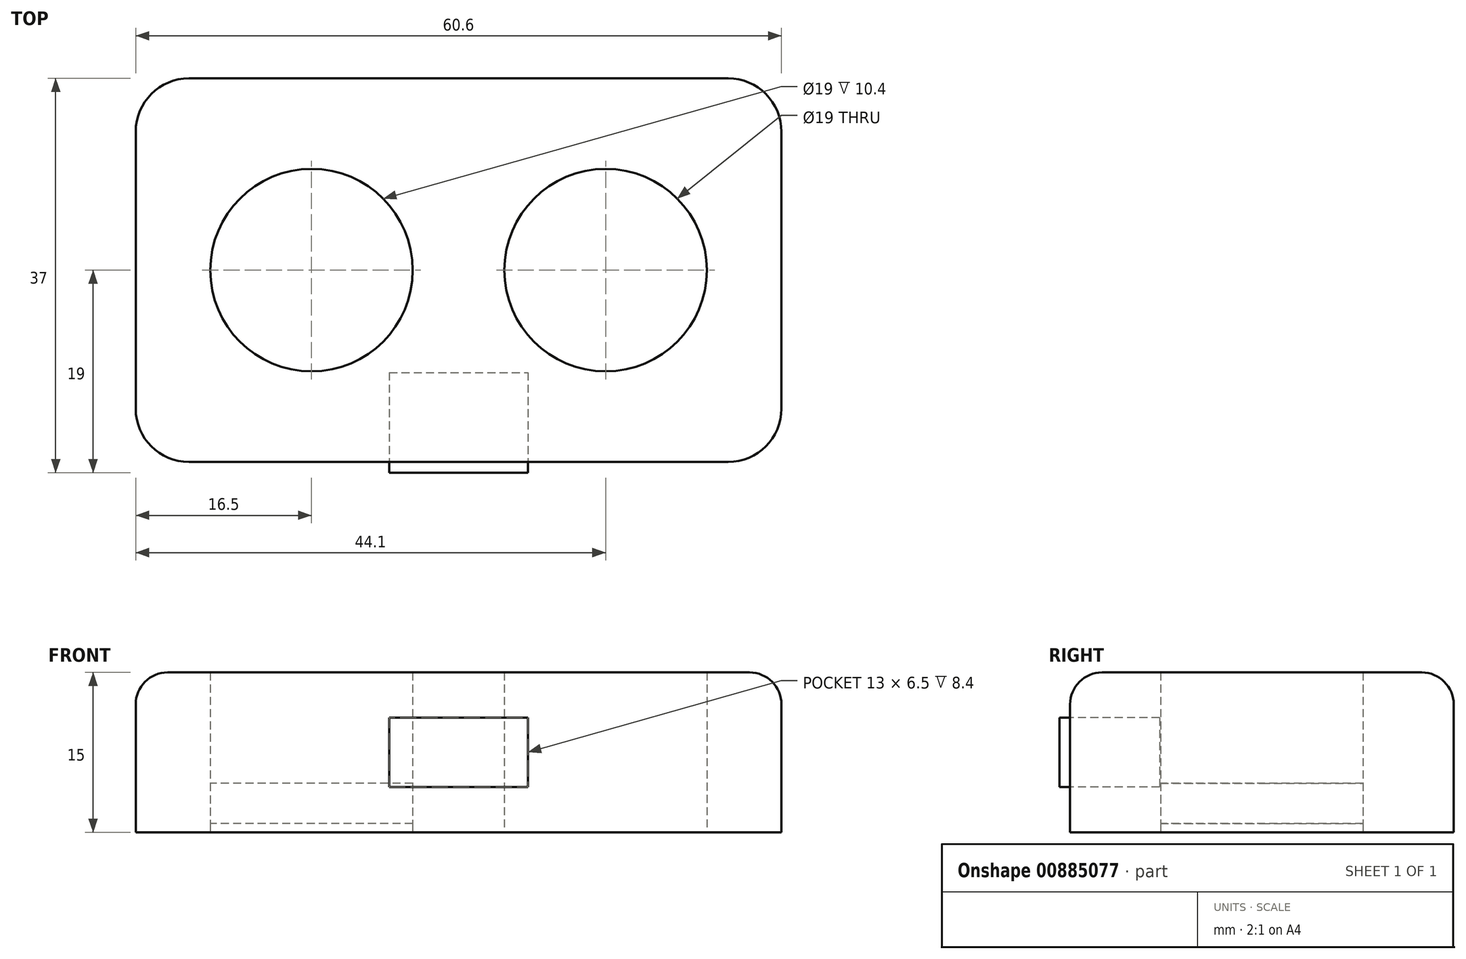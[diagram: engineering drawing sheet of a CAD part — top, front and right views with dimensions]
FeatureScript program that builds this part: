
annotation { "Feature Type Name" : "Feature", "Feature Type Description" : "" }
export const myFeature = defineFeature(function(context is Context, id is Id, definition is map)
    precondition{}
    {
        {
            var Q0;
            Q0=qCreatedBy(makeId("Top.planeOp"),FACE);
            var sketch = newSketch(context, id + "F0", { "sketchPlane" : qUnion([Q0])});
            skLineSegment(sketch, "E0.bottom", {"start": v(-23.3, 16) * mm, "end": v(23.3, 16) * mm});
            skLineSegment(sketch, "E0.top", {"start": v(-23.3, -16) * mm, "end": v(23.3, -16) * mm});
            skLineSegment(sketch, "E0.left", {"start": v(-28.3, 11) * mm, "end": v(-28.3, -11) * mm});
            skLineSegment(sketch, "E0.right", {"start": v(28.3, 11) * mm, "end": v(28.3, -11) * mm});
            skPoint(sketch, "E0.middle", {"position": v(0, 0) * mm});
            skLineSegment(sketch, "E1.0", {"start": v(-25.3, 18) * mm, "end": v(25.3, 18) * mm});
            skLineSegment(sketch, "E1.1", {"start": v(-30.3, 13) * mm, "end": v(-30.3, -13) * mm});
            skLineSegment(sketch, "E1.2", {"start": v(-25.3, -18) * mm, "end": v(25.3, -18) * mm});
            skLineSegment(sketch, "E1.3", {"start": v(30.3, 13) * mm, "end": v(30.3, -13) * mm});
            skCircle(sketch, "E2", {"center": v(-13.8, 0) * mm, "radius": 9.5 * mm});
            skCircle(sketch, "E3.MirrorC", {"center": v(13.8, 0) * mm, "radius": 9.5 * mm});
            skPoint(sketch, "E4.visualSharp", {"position": v(-30.3, 18) * mm});
            skArc(sketch, "E4.filletArc", {"start": v(-25.3, 18) * mm, "mid": v(-28.84, 16.54) * mm, "end": v(-30.3, 13) * mm});
            skPoint(sketch, "E5.visualSharp", {"position": v(-30.3, -18) * mm});
            skArc(sketch, "E5.filletArc", {"start": v(-30.3, -13) * mm, "mid": v(-28.84, -16.54) * mm, "end": v(-25.3, -18) * mm});
            skPoint(sketch, "E6.visualSharp", {"position": v(30.3, -18) * mm});
            skArc(sketch, "E6.filletArc", {"start": v(25.3, -18) * mm, "mid": v(28.84, -16.54) * mm, "end": v(30.3, -13) * mm});
            skPoint(sketch, "E7.visualSharp", {"position": v(30.3, 18) * mm});
            skArc(sketch, "E7.filletArc", {"start": v(30.3, 13) * mm, "mid": v(28.84, 16.54) * mm, "end": v(25.3, 18) * mm});
            skPoint(sketch, "E8.visualSharp", {"position": v(28.3, 16) * mm});
            skArc(sketch, "E8.filletArc", {"start": v(28.3, 11) * mm, "mid": v(26.84, 14.54) * mm, "end": v(23.3, 16) * mm});
            skPoint(sketch, "E9.visualSharp", {"position": v(28.3, -16) * mm});
            skArc(sketch, "E9.filletArc", {"start": v(23.3, -16) * mm, "mid": v(26.84, -14.54) * mm, "end": v(28.3, -11) * mm});
            skPoint(sketch, "E10.visualSharp", {"position": v(-28.3, -16) * mm});
            skArc(sketch, "E10.filletArc", {"start": v(-28.3, -11) * mm, "mid": v(-26.84, -14.54) * mm, "end": v(-23.3, -16) * mm});
            skPoint(sketch, "E11.visualSharp", {"position": v(-28.3, 16) * mm});
            skArc(sketch, "E11.filletArc", {"start": v(-23.3, 16) * mm, "mid": v(-26.84, 14.54) * mm, "end": v(-28.3, 11) * mm});
            skSolve(sketch);
        }
        {
            var Q0;
            Q0=makeQuery(id+"F0.imprint","IMPRINT",FACE,{"disambiguationData":[TD([[makeQuery(id+"F0.imprint","IMPRINT",EDGE,{"derivedFrom":sQuery(id+"F0.wireOp",EDGE,"E0.bottom")}),-1.0]])]});
            var Q1;
            Q1=makeQuery(id+"F0.imprint","IMPRINT",FACE,{"disambiguationData":[TD([[makeQuery(id+"F0.imprint","IMPRINT",EDGE,{"derivedFrom":sQuery(id+"F0.wireOp",EDGE,"E0.bottom")}),1.0]])]});
            extrude(context, id + "F1", {"entities" : qUnion([Q0, Q1]), "depth" : 15 * mm, "offsetDistance" : 25 * mm});
        }
        {
            var Q0;
            Q0=makeQuery(id+"F0.imprint","IMPRINT",FACE,{"disambiguationData":[TD([[makeQuery(id+"F0.imprint","IMPRINT",EDGE,{"derivedFrom":sQuery(id+"F0.wireOp",EDGE,"E2")}),1.0]])]});
            var Q1;
            Q1=makeQuery(id+"F0.imprint","IMPRINT",FACE,{"disambiguationData":[TD([[makeQuery(id+"F0.imprint","IMPRINT",EDGE,{"derivedFrom":sQuery(id+"F0.wireOp",EDGE,"E3.MirrorC")}),-1.0]])]});
            extrude(context, id + "F2", {"entities" : qUnion([Q0, Q1]), "operationType" : NewBodyOperationType.ADD, "depth" : 1 * mm, "offsetDistance" : 25 * mm});
        }
        {
            var Q0;
            Q0=makeQuery(id+"F1.opExtrude","SWEPT_FACE",FACE,{"disambiguationData":[OSD([sQuery(id+"F0.wireOp",EDGE,"E1.2")])]});
            var sketch = newSketch(context, id + "F3", { "sketchPlane" : qUnion([Q0])});
            skPoint(sketch, "E12", {"position": v(0, 7.5) * mm});
            skLineSegment(sketch, "E13", {"start": v(0, 15) * mm, "end": v(0, 0) * mm});
            skPoint(sketch, "E13.startSnap0", {"position": v(0, 15) * mm});
            skLineSegment(sketch, "E14.bottom", {"start": v(-6.5, 10.75) * mm, "end": v(6.5, 10.75) * mm});
            skLineSegment(sketch, "E14.top", {"start": v(-6.5, 4.25) * mm, "end": v(6.5, 4.25) * mm});
            skLineSegment(sketch, "E14.left", {"start": v(-6.5, 10.75) * mm, "end": v(-6.5, 4.25) * mm});
            skLineSegment(sketch, "E14.right", {"start": v(6.5, 10.75) * mm, "end": v(6.5, 4.25) * mm});
            skSolve(sketch);
        }
        {
            var Q0;
            {var subQ5=sQuery(id+"F3.wireOp",EDGE,"E14.left");Q0=makeQuery(id+"F3.imprint","IMPRINT",FACE,{"disambiguationData":[TD([[makeQuery(id+"F3.imprint","IMPRINT",EDGE,{"derivedFrom":subQ5}),1.0]])]});}
            var Q1;
            {var subQ5=sQuery(id+"F3.wireOp",EDGE,"E14.right");Q1=makeQuery(id+"F3.imprint","IMPRINT",FACE,{"disambiguationData":[TD([[makeQuery(id+"F3.imprint","IMPRINT",EDGE,{"derivedFrom":subQ5}),-1.0]])]});}
            extrude(context, id + "F4", {"entities" : qUnion([Q0, Q1]), "operationType" : NewBodyOperationType.REMOVE, "oppositeDirection" : true, "depth" : 8.4 * mm, "offsetDistance" : 25 * mm});
        }
        {
            var Q0;
            Q0=makeQuery(id+"F1.opExtrude","CAP_EDGE",EDGE,{"disambiguationData":[OSD([sQuery(id+"F0.wireOp",EDGE,"E1.2")])],"isStart":false});
            fillet(context, id + "F5", {"entities" : qUnion([Q0]), "radius" : 3 * mm, "tangentPropagation" : true, "allowEdgeOverflow" : false});
        }
        {
            var Q0;
            Q0=makeQuery(id+"F0.imprint","IMPRINT",FACE,{"disambiguationData":[TD([[makeQuery(id+"F0.imprint","IMPRINT",EDGE,{"derivedFrom":sQuery(id+"F0.wireOp",EDGE,"E2")}),1.0]])]});
            extrude(context, id + "F6", {"entities" : qUnion([Q0]), "depth" : .8 * mm, "offsetDistance" : 25 * mm});
        }
        {
            var Q0;
            {var subQ5=sQuery(id+"F3.wireOp",EDGE,"E14.right");Q0=makeQuery(id+"F3.imprint","IMPRINT",FACE,{"disambiguationData":[TD([[makeQuery(id+"F3.imprint","IMPRINT",EDGE,{"derivedFrom":subQ5}),-1.0]])]});}
            var Q1;
            {var subQ5=sQuery(id+"F3.wireOp",EDGE,"E14.left");Q1=makeQuery(id+"F3.imprint","IMPRINT",FACE,{"disambiguationData":[TD([[makeQuery(id+"F3.imprint","IMPRINT",EDGE,{"derivedFrom":subQ5}),1.0]])]});}
            extrude(context, id + "F7", {"entities" : qUnion([Q0, Q1]), "depth" : 1 * mm, "offsetDistance" : 25 * mm});
        }
        {
            var Q0;
            Q0=makeQuery(id+"F0.imprint","IMPRINT",FACE,{"disambiguationData":[TD([[makeQuery(id+"F0.imprint","IMPRINT",EDGE,{"derivedFrom":sQuery(id+"F0.wireOp",EDGE,"E2")}),1.0]])]});
            extrude(context, id + "F8", {"entities" : qUnion([Q0]), "depth" : 4.6 * mm, "offsetDistance" : 25 * mm});
        }
    });
